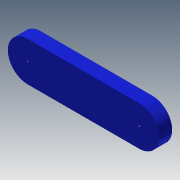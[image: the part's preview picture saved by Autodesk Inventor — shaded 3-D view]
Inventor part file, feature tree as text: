
AUTODESK INVENTOR PART (.ipt)
format: ipt  version: 2013 (Build 170138000, 138)  size: 101,888 bytes
history: native  units: mm
features: extrude x3, sketch x3
ambient origin geometry x8: Origin, YZ Plane, XZ Plane, XY Plane, X Axis, Y Axis, Z Axis, Center Point
bodies: Solid1 (feature_tree)
feature tree (6):
  extrude  "Extrusion1"  Depth=6.0mm
  extrude  "Extrusion2"  Depth=6.0mm
  extrude  "Extrusion3"  Depth=3.0mm
  sketch  "Sketch1"  dims[d0=17.0mm d1=6.0mm]
  sketch  "Sketch2"  dims[d2=6.0mm d3=6.0mm]
  sketch  "Sketch3"  dims[d4=2.0mm d5=0.0mm d6=3.0mm d7=3.0mm d8=2.0mm d9=0.0mm d10=0.2mm d11=0.2mm d12=2.0mm d13=0.0mm]
